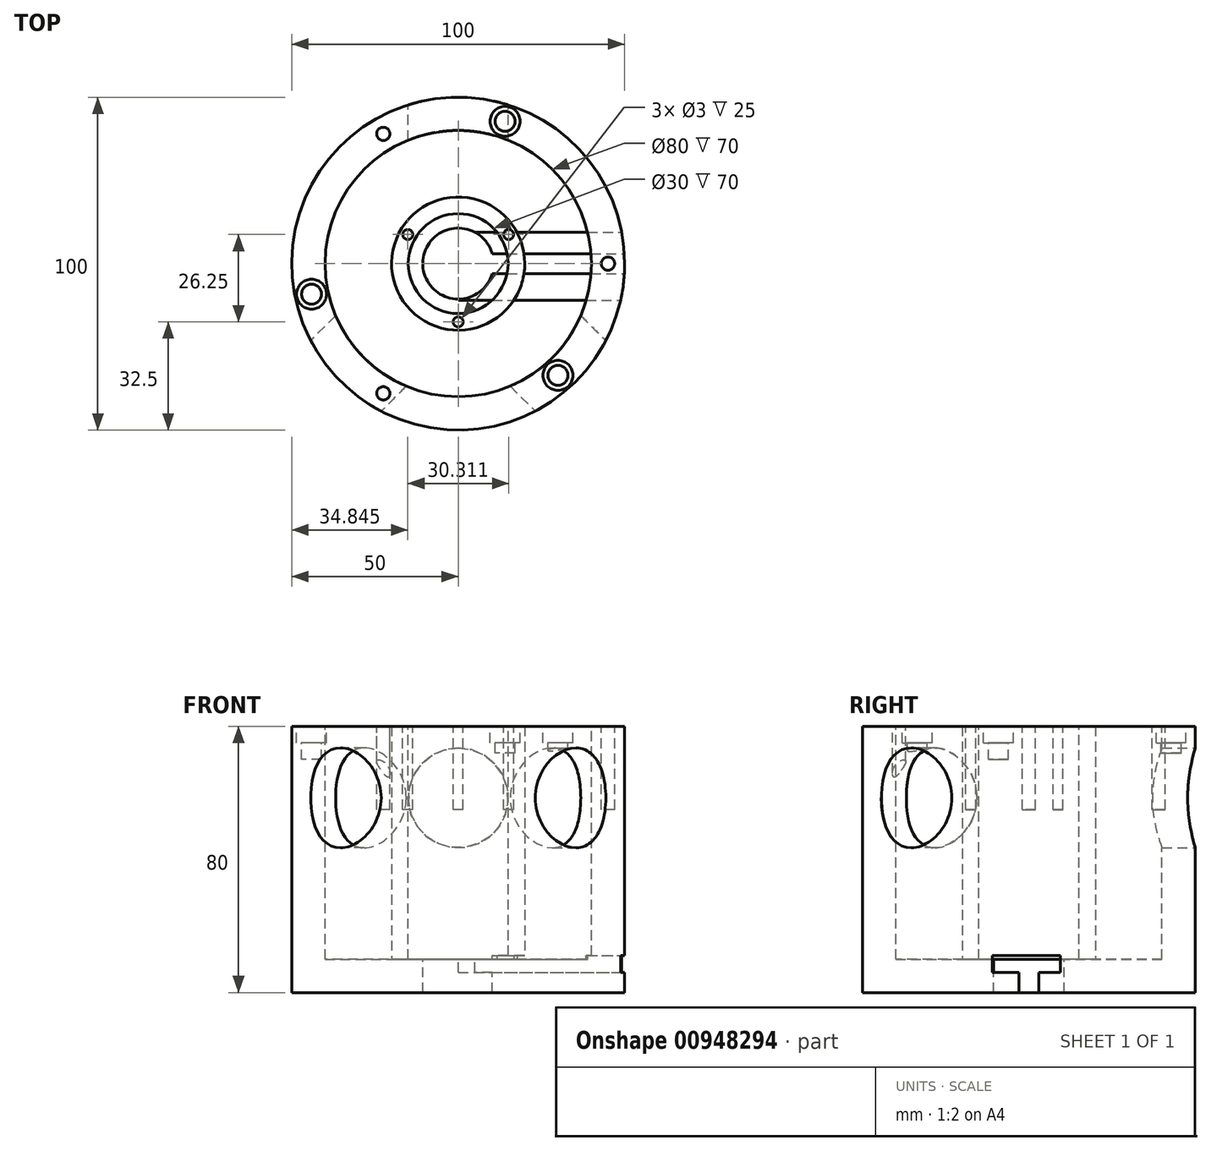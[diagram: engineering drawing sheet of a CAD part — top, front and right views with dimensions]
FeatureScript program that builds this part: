
annotation { "Feature Type Name" : "Feature", "Feature Type Description" : "" }
export const myFeature = defineFeature(function(context is Context, id is Id, definition is map)
    precondition{}
    {
        {
            var Q0;
            Q0=qCreatedBy(makeId("Top.planeOp"),FACE);
            var sketch = newSketch(context, id + "F0", { "sketchPlane" : qUnion([Q0])});
            skCircle(sketch, "E0", {"center": v(0, 0) * mm, "radius": 50 * mm});
            skSolve(sketch);
        }
        {
            var Q0;
            Q0 = qSketchRegion(id + "F0", true);
            extrude(context, id + "F1", {"entities" : qUnion([Q0]), "endBound" : BoundingType.SYMMETRIC, "depth" : 80 * mm, "offsetDistance" : 25 * mm});
        }
        {
            var Q0;
            Q0=makeQuery(id+"F1.opExtrude","CAP_FACE",FACE,{"disambiguationData":[OSD([sQuery(id+"F0.wireOp",EDGE,"E0")])],"isStart":false});
            var sketch = newSketch(context, id + "F2", { "sketchPlane" : qUnion([Q0])});
            skCircle(sketch, "E1", {"center": v(0, 0) * mm, "radius": 40 * mm});
            skSolve(sketch);
        }
        {
            var Q0;
            Q0 = qSketchRegion(id + "F2", true);
            extrude(context, id + "F3", {"entities" : qUnion([Q0]), "operationType" : NewBodyOperationType.REMOVE, "oppositeDirection" : true, "depth" : 70 * mm, "offsetDistance" : 25 * mm});
        }
        {
            var Q0;
            Q0=makeQuery(id+"F3.boolean.opBoolean","COPY",FACE,{"derivedFrom":makeQuery(id+"F3.opExtrude","CAP_FACE",FACE,{"disambiguationData":[OSD([sQuery(id+"F2.wireOp",EDGE,"E1")])],"isStart":false})});
            var sketch = newSketch(context, id + "F4", { "sketchPlane" : qUnion([Q0])});
            skCircle(sketch, "E2", {"center": v(0, 0) * mm, "radius": 20 * mm});
            skSolve(sketch);
        }
        {
            var Q0;
            Q0 = qSketchRegion(id + "F4", true);
            extrude(context, id + "F5", {"entities" : qUnion([Q0]), "operationType" : NewBodyOperationType.ADD, "depth" : 70 * mm, "offsetDistance" : 25 * mm});
        }
        {
            var Q0;
            Q0=makeQuery(id+"F5.opExtrude","CAP_FACE",FACE,{"disambiguationData":[OSD([sQuery(id+"F4.wireOp",EDGE,"E2")])],"isStart":false});
            var sketch = newSketch(context, id + "F6", { "sketchPlane" : qUnion([Q0])});
            skCircle(sketch, "E3", {"center": v(0, 0) * mm, "radius": 15 * mm});
            skSolve(sketch);
        }
        {
            var Q0;
            Q0 = qSketchRegion(id + "F6", true);
            extrude(context, id + "F7", {"entities" : qUnion([Q0]), "operationType" : NewBodyOperationType.REMOVE, "oppositeDirection" : true, "depth" : 70 * mm, "offsetDistance" : 25 * mm});
        }
        {
            var Q0;
            Q0=makeQuery(id+"F1.opExtrude","CAP_FACE",FACE,{"disambiguationData":[OSD([sQuery(id+"F0.wireOp",EDGE,"E0")])],"isStart":false});
            var sketch = newSketch(context, id + "F8", { "sketchPlane" : qUnion([Q0])});
            skLineSegment(sketch, "E4", {"start": v(0, 0) * mm, "end": v(15.65, 47.49) * mm, "construction": true});
            skLineSegment(sketch, "E5", {"start": v(0, 0) * mm, "end": v(33.3, -37.3) * mm, "construction": true});
            skLineSegment(sketch, "E6", {"start": v(0, 0) * mm, "end": v(-48.95, -10.2) * mm, "construction": true});
            skCircle(sketch, "E7", {"center": v(0, 0) * mm, "radius": 45 * mm, "construction": true});
            skCircle(sketch, "E8", {"center": v(14.08, 42.74) * mm, "radius": 4.5 * mm});
            skCircle(sketch, "E9", {"center": v(-44.05, -9.17) * mm, "radius": 4.5 * mm});
            skCircle(sketch, "E10", {"center": v(29.97, -33.57) * mm, "radius": 4.5 * mm});
            skSolve(sketch);
        }
        {
            var Q0;
            Q0=makeQuery(id+"F8.imprint","IMPRINT",FACE,{"disambiguationData":[TD([[makeQuery(id+"F8.imprint","IMPRINT",EDGE,{"derivedFrom":sQuery(id+"F8.wireOp",EDGE,"E9")}),1.0]])]});
            var Q1;
            Q1=makeQuery(id+"F8.imprint","IMPRINT",FACE,{"disambiguationData":[TD([[makeQuery(id+"F8.imprint","IMPRINT",EDGE,{"derivedFrom":sQuery(id+"F8.wireOp",EDGE,"E10")}),1.0]])]});
            var Q2;
            Q2=makeQuery(id+"F8.imprint","IMPRINT",FACE,{"disambiguationData":[TD([[makeQuery(id+"F8.imprint","IMPRINT",EDGE,{"derivedFrom":sQuery(id+"F8.wireOp",EDGE,"E8")}),1.0]])]});
            extrude(context, id + "F9", {"entities" : qUnion([Q0, Q1, Q2]), "operationType" : NewBodyOperationType.REMOVE, "oppositeDirection" : true, "depth" : 5 * mm, "offsetDistance" : 25 * mm});
        }
        {
            var Q0;
            Q0=makeQuery(id+"F9.boolean.opBoolean","COPY",FACE,{"derivedFrom":makeQuery(id+"F9.opExtrude","CAP_FACE",FACE,{"disambiguationData":[OSD([sQuery(id+"F8.wireOp",EDGE,"E8")])],"isStart":false})});
            var sketch = newSketch(context, id + "F10", { "sketchPlane" : qUnion([Q0])});
            skCircle(sketch, "E11", {"center": v(14.08, 42.74) * mm, "radius": 3 * mm});
            skSolve(sketch);
        }
        {
            var Q0;
            Q0 = qSketchRegion(id + "F10", true);
            extrude(context, id + "F11", {"entities" : qUnion([Q0]), "operationType" : NewBodyOperationType.REMOVE, "oppositeDirection" : true, "depth" : 3 * mm, "offsetDistance" : 25 * mm});
        }
        {
            var Q0;
            Q0=makeQuery(id+"F9.boolean.opBoolean","COPY",FACE,{"derivedFrom":makeQuery(id+"F9.opExtrude","CAP_FACE",FACE,{"disambiguationData":[OSD([sQuery(id+"F8.wireOp",EDGE,"E9")])],"isStart":false})});
            var sketch = newSketch(context, id + "F12", { "sketchPlane" : qUnion([Q0])});
            skCircle(sketch, "E12", {"center": v(-44.05, -9.17) * mm, "radius": 3 * mm});
            skSolve(sketch);
        }
        {
            var Q0;
            Q0 = qSketchRegion(id + "F12", true);
            extrude(context, id + "F13", {"entities" : qUnion([Q0]), "operationType" : NewBodyOperationType.REMOVE, "oppositeDirection" : true, "depth" : 5 * mm, "offsetDistance" : 25 * mm});
        }
        {
            var Q0;
            Q0=makeQuery(id+"F9.boolean.opBoolean","COPY",FACE,{"derivedFrom":makeQuery(id+"F9.opExtrude","CAP_FACE",FACE,{"disambiguationData":[OSD([sQuery(id+"F8.wireOp",EDGE,"E10")])],"isStart":false})});
            var sketch = newSketch(context, id + "F14", { "sketchPlane" : qUnion([Q0])});
            skCircle(sketch, "E13", {"center": v(29.97, -33.57) * mm, "radius": 3 * mm});
            skSolve(sketch);
        }
        {
            var Q0;
            Q0 = qSketchRegion(id + "F14", true);
            extrude(context, id + "F15", {"entities" : qUnion([Q0]), "operationType" : NewBodyOperationType.REMOVE, "depth" : 5 * mm, "offsetDistance" : 25 * mm});
        }
        {
            var Q0;
            Q0 = qSketchRegion(id + "F14", true);
            extrude(context, id + "F16", {"entities" : qUnion([Q0]), "operationType" : NewBodyOperationType.REMOVE, "oppositeDirection" : true, "depth" : 5 * mm, "offsetDistance" : 25 * mm});
        }
        {
            var Q0;
            Q0=makeQuery(id+"F1.opExtrude","CAP_FACE",FACE,{"disambiguationData":[OSD([sQuery(id+"F0.wireOp",EDGE,"E0")])],"isStart":false});
            var sketch = newSketch(context, id + "F17", { "sketchPlane" : qUnion([Q0])});
            skLineSegment(sketch, "E14", {"start": v(0, 0) * mm, "end": v(-25, 43.3) * mm, "construction": true});
            skLineSegment(sketch, "E15", {"start": v(0, 0) * mm, "end": v(-25, -43.3) * mm, "construction": true});
            skLineSegment(sketch, "E16", {"start": v(0, 0) * mm, "end": v(50, 0) * mm, "construction": true});
            skCircle(sketch, "E17", {"center": v(0, 0) * mm, "radius": 45 * mm, "construction": true});
            skCircle(sketch, "E18", {"center": v(-22.5, 38.97) * mm, "radius": 2 * mm});
            skCircle(sketch, "E19", {"center": v(-22.5, -38.97) * mm, "radius": 2 * mm});
            skCircle(sketch, "E20", {"center": v(45, 0) * mm, "radius": 2 * mm});
            skSolve(sketch);
        }
        {
            var Q0;
            Q0 = qSketchRegion(id + "F17", true);
            extrude(context, id + "F18", {"entities" : qUnion([Q0]), "operationType" : NewBodyOperationType.REMOVE, "oppositeDirection" : true, "depth" : 25 * mm, "offsetDistance" : 25 * mm});
        }
        {
            var Q0;
            Q0=makeQuery(id+"F5.opExtrude","CAP_FACE",FACE,{"disambiguationData":[OSD([sQuery(id+"F4.wireOp",EDGE,"E2")])],"isStart":false});
            var sketch = newSketch(context, id + "F19", { "sketchPlane" : qUnion([Q0])});
            skLineSegment(sketch, "E21", {"start": v(0, 0) * mm, "end": v(17.32, 10) * mm, "construction": true});
            skLineSegment(sketch, "E22", {"start": v(0, 0) * mm, "end": v(-17.32, 10) * mm, "construction": true});
            skLineSegment(sketch, "E23", {"start": v(0, 0) * mm, "end": v(0, -20) * mm, "construction": true});
            skCircle(sketch, "E24", {"center": v(0, 0) * mm, "radius": 17.5 * mm, "construction": true});
            skCircle(sketch, "E25", {"center": v(-15.16, 8.75) * mm, "radius": 1.5 * mm});
            skCircle(sketch, "E26", {"center": v(15.16, 8.75) * mm, "radius": 1.5 * mm});
            skCircle(sketch, "E27", {"center": v(0, -17.5) * mm, "radius": 1.5 * mm});
            skSolve(sketch);
        }
        {
            var Q0;
            Q0 = qSketchRegion(id + "F19", true);
            extrude(context, id + "F20", {"entities" : qUnion([Q0]), "operationType" : NewBodyOperationType.REMOVE, "oppositeDirection" : true, "depth" : 25 * mm, "offsetDistance" : 25 * mm});
        }
        {
            var Q0;
            Q0=qCreatedBy(makeId("Front.planeOp"),FACE);
            cPlane(context, id + "F21", {"entities" : qUnion([Q0]), "cplaneType" : CPlaneType.OFFSET, "offset" : 50 * mm, "oppositeDirection" : true, "width" : 150 * mm, "height" : 150 * mm});
        }
        {
            var Q0;
            Q0=qCreatedBy(id+"F21.planeOp",FACE);
            var sketch = newSketch(context, id + "F22", { "sketchPlane" : qUnion([Q0])});
            skLineSegment(sketch, "E28", {"start": v(-72.71, 0) * mm, "end": v(72.27, 0) * mm, "construction": true});
            skLineSegment(sketch, "E29", {"start": v(0, 0) * mm, "end": v(0, 72.82) * mm, "construction": true});
            skCircle(sketch, "E30", {"center": v(0, 18.5) * mm, "radius": 15 * mm});
            skSolve(sketch);
        }
        {
            var Q0;
            Q0 = qSketchRegion(id + "F22", true);
            extrude(context, id + "F23", {"entities" : qUnion([Q0]), "operationType" : NewBodyOperationType.REMOVE, "depth" : 15 * mm, "offsetDistance" : 25 * mm});
        }
        {
            var Q0;
            Q0=qCreatedBy(makeId("Front.planeOp"),FACE);
            var Q1;
            Q1=qCreatedBy(makeId("Right.planeOp"),FACE);
            cPlane(context, id + "F24", {"entities" : qUnion([Q0, Q1]), "cplaneType" : CPlaneType.MID_PLANE, "offset" : 25 * mm, "width" : 150 * mm, "height" : 150 * mm});
        }
        {
            var Q0;
            Q0=qCreatedBy(id+"F24.planeOp",FACE);
            cPlane(context, id + "F25", {"entities" : qUnion([Q0]), "cplaneType" : CPlaneType.OFFSET, "offset" : 50 * mm, "width" : 150 * mm, "height" : 150 * mm});
        }
        {
            var Q0;
            Q0=qCreatedBy(id+"F25.planeOp",FACE);
            var sketch = newSketch(context, id + "F26", { "sketchPlane" : qUnion([Q0])});
            skLineSegment(sketch, "E31", {"start": v(-70.99, 0) * mm, "end": v(73.52, 0) * mm, "construction": true});
            skLineSegment(sketch, "E32", {"start": v(0, 0) * mm, "end": v(0, 80.32) * mm, "construction": true});
            skCircle(sketch, "E33", {"center": v(0, 18.5) * mm, "radius": 15 * mm});
            skSolve(sketch);
        }
        {
            var Q0;
            Q0 = qSketchRegion(id + "F26", true);
            extrude(context, id + "F27", {"entities" : qUnion([Q0]), "operationType" : NewBodyOperationType.REMOVE, "oppositeDirection" : true, "depth" : 25 * mm, "offsetDistance" : 25 * mm});
        }
        {
            var Q0;
            Q0=qCreatedBy(makeId("Right.planeOp"),FACE);
            cPlane(context, id + "F28", {"entities" : qUnion([Q0]), "cplaneType" : CPlaneType.OFFSET, "offset" : 50 * mm, "width" : 150 * mm, "height" : 150 * mm});
        }
        {
            var Q0;
            Q0=qCreatedBy(id+"F21.planeOp",FACE);
            cPlane(context, id + "F29", {"entities" : qUnion([Q0]), "cplaneType" : CPlaneType.OFFSET, "offset" : 100 * mm, "width" : 150 * mm, "height" : 150 * mm});
        }
        {
            var Q0;
            Q0=qCreatedBy(makeId("Front.planeOp"),FACE);
            var Q1;
            Q1=qCreatedBy(makeId("Right.planeOp"),FACE);
            cPlane(context, id + "F30", {"entities" : qUnion([Q0, Q1]), "cplaneType" : CPlaneType.MID_PLANE, "offset" : 25 * mm, "flipAlignment" : true, "width" : 150 * mm, "height" : 150 * mm});
        }
        {
            var Q0;
            Q0=qCreatedBy(id+"F30.planeOp",FACE);
            cPlane(context, id + "F31", {"entities" : qUnion([Q0]), "cplaneType" : CPlaneType.OFFSET, "offset" : 50 * mm, "width" : 150 * mm, "height" : 150 * mm});
        }
        {
            var Q0;
            Q0=qCreatedBy(id+"F31.planeOp",FACE);
            var sketch = newSketch(context, id + "F32", { "sketchPlane" : qUnion([Q0])});
            skLineSegment(sketch, "E34", {"start": v(83.12, 0) * mm, "end": v(-51.7, 0) * mm, "construction": true});
            skLineSegment(sketch, "E35", {"start": v(0, 0) * mm, "end": v(0, 61.76) * mm, "construction": true});
            skCircle(sketch, "E36", {"center": v(0, 18.5) * mm, "radius": 15 * mm});
            skSolve(sketch);
        }
        {
            var Q0;
            Q0 = qSketchRegion(id + "F32", true);
            extrude(context, id + "F33", {"entities" : qUnion([Q0]), "operationType" : NewBodyOperationType.REMOVE, "oppositeDirection" : true, "depth" : 25 * mm, "offsetDistance" : 25 * mm});
        }
        {
            var Q0;
            Q0=qCreatedBy(id+"F28.planeOp",FACE);
            var sketch = newSketch(context, id + "F34", { "sketchPlane" : qUnion([Q0])});
            skLineSegment(sketch, "E37", {"start": v(0, 0) * mm, "end": v(0, -12.47) * mm, "construction": true});
            skLineSegment(sketch, "E38", {"start": v(-3, -40) * mm, "end": v(0, -40) * mm});
            skLineSegment(sketch, "E39", {"start": v(0, -40) * mm, "end": v(3, -40) * mm});
            skLineSegment(sketch, "E40", {"start": v(-3, -40) * mm, "end": v(-3, -33.96) * mm});
            skLineSegment(sketch, "E41", {"start": v(-3, -33.96) * mm, "end": v(-10.99, -33.96) * mm});
            skLineSegment(sketch, "E42", {"start": v(-10.99, -33.96) * mm, "end": v(-10.99, -28.85) * mm});
            skLineSegment(sketch, "E43", {"start": v(-10.99, -28.85) * mm, "end": v(9.4, -28.85) * mm});
            skLineSegment(sketch, "E44", {"start": v(9.4, -28.85) * mm, "end": v(9.4, -33.96) * mm});
            skLineSegment(sketch, "E45", {"start": v(9.4, -33.96) * mm, "end": v(3, -33.96) * mm});
            skLineSegment(sketch, "E46", {"start": v(3, -33.96) * mm, "end": v(3, -40) * mm});
            skSolve(sketch);
        }
        {
            var Q0;
            Q0 = qSketchRegion(id + "F34", true);
            extrude(context, id + "F35", {"entities" : qUnion([Q0]), "operationType" : NewBodyOperationType.REMOVE, "oppositeDirection" : true, "depth" : 50 * mm, "offsetDistance" : 25 * mm});
        }
        {
            var Q0;
            Q0=makeQuery(id+"F7.boolean.opBoolean","COPY",FACE,{"derivedFrom":makeQuery(id+"F7.opExtrude","CAP_FACE",FACE,{"disambiguationData":[OSD([sQuery(id+"F6.wireOp",EDGE,"E3")])],"isStart":false})});
            var sketch = newSketch(context, id + "F36", { "sketchPlane" : qUnion([Q0])});
            skCircle(sketch, "E47", {"center": v(0, 0) * mm, "radius": 10.65 * mm});
            skSolve(sketch);
        }
        {
            var Q0;
            Q0 = qSketchRegion(id + "F36", true);
            extrude(context, id + "F37", {"entities" : qUnion([Q0]), "operationType" : NewBodyOperationType.REMOVE, "oppositeDirection" : true, "depth" : 25 * mm, "offsetDistance" : 25 * mm});
        }
    });
